# Revit family: Towel_Ring-Grohe-Essentials-40365_Series
name_source: partatom
category: Specialty Equipment
units: mm (PartAtom-declared; Revit-internal decimal feet)

## family parameters
Cut with Voids When Loaded = No
Host = Face
OmniClass Number = 23.40.20.21.27
OmniClass Title = Towel Bars
Part Type = Normal
Room Calculation Point = No
Round Connector Dimension = Use Diameter
Shared = Yes

## types (5) — shared parameters
Assembly Code = C1030200
Default Elevation = 1016 mm
Description = Essentials Towel Ring
Height = 201 mm  [stored 0.659449 ft]
Installation Instruction Link = https://americanstandard.box.com
Installation Type = Wall Mounted
Length = 44 mm
Manufacturer = Grohe
Price = Prices may vary. Please consult Manufacturer Representative for most up-to-date price list.
Product Documentation Link = https://americanstandard.box.com
Product Page URL = https://www.grohe.us
Revised Date = 11/01/2021
URL = https://www.grohe.us
Width = 180 mm  [stored 0.590551 ft]

## per-type parameters (varying)
| type | Finish | Material | Model |
| 40365A01 | Metal-Grohe-GN1-Brushed Cool Sunset | Metal-Grohe-GN1-Brushed Cool Sunset | 40365GN1 |
| 40365GN1 | Metal-Grohe-GN1-Brushed Cool Sunset | Metal-Grohe-GN1-Brushed Cool Sunset | 40365GN1 |
| 40365BE1 | Metal-Grohe-BE1-Polished Nickel Infinity Finish | Metal-Grohe-BE1-Polished Nickel Infinity Finish | 40365BE1 |
| 40365001 | Metal-Grohe-001-StarLight Chrome | Metal-Grohe-001-StarLight Chrome | 40365001 |
| 40365EN1 | Metal-Grohe-EN1-Brushed Nickel Infinity Finish | Metal-Grohe-EN1-Brushed Nickel Infinity Finish | 40365EN1 |

note: [stored X ft] marks values corroborated as IEEE doubles in the binary element streams (Revit-internal decimal feet)

## geometry (parser evidence)
native form markers: Sweep x5
no freeform markers — native parametric forms only
